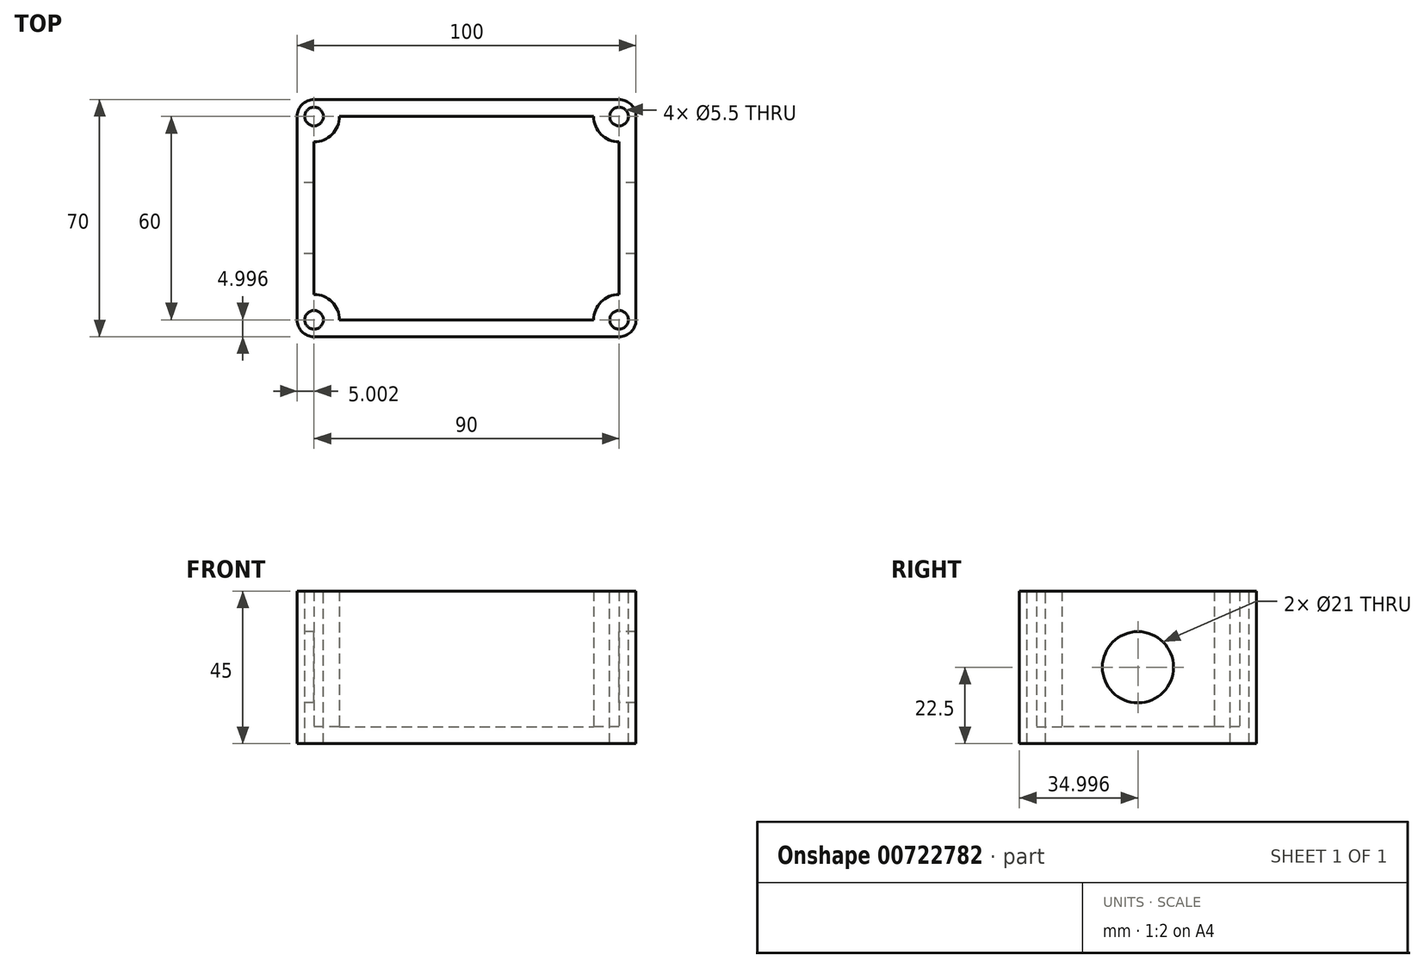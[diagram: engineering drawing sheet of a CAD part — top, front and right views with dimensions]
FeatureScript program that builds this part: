
annotation { "Feature Type Name" : "Feature", "Feature Type Description" : "" }
export const myFeature = defineFeature(function(context is Context, id is Id, definition is map)
    precondition{}
    {
        {
            var Q0;
            Q0=qCreatedBy(makeId("Top.planeOp"),FACE);
            var sketch = newSketch(context, id + "F0", { "sketchPlane" : qUnion([Q0])});
            skLineSegment(sketch, "E0.bottom", {"start": v(-50.44, 34.5) * mm, "end": v(49.56, 34.5) * mm});
            skLineSegment(sketch, "E0.top", {"start": v(-50.44, -35.5) * mm, "end": v(49.56, -35.5) * mm});
            skLineSegment(sketch, "E0.left", {"start": v(-50.44, 34.5) * mm, "end": v(-50.44, -35.5) * mm});
            skLineSegment(sketch, "E0.right", {"start": v(49.56, 34.5) * mm, "end": v(49.56, -35.5) * mm});
            skSolve(sketch);
        }
        {
            var Q0;
            Q0 = qSketchRegion(id + "F0", true);
            extrude(context, id + "F1", {"entities" : qUnion([Q0]), "depth" : 45 * mm, "offsetDistance" : 25 * mm});
        }
        {
            var Q0;
            Q0=makeQuery(id+"F1.opExtrude","CAP_FACE",FACE,{"disambiguationData":[OSD([sQuery(id+"F0.wireOp",EDGE,"E0.bottom"),sQuery(id+"F0.wireOp",EDGE,"E0.top"),sQuery(id+"F0.wireOp",EDGE,"E0.left"),sQuery(id+"F0.wireOp",EDGE,"E0.right")])],"isStart":false});
            shell(context, id + "F2", {"entities" : qUnion([Q0]), "thickness" : 5 * mm});
        }
        {
            var Q0;
            Q0=makeQuery(id+"F2.opShell","OFFSET_FACE",FACE,{"disambiguationData":[OSD([sQuery(id+"F0.wireOp",EDGE,"E0.bottom"),sQuery(id+"F0.wireOp",EDGE,"E0.top"),sQuery(id+"F0.wireOp",EDGE,"E0.left"),sQuery(id+"F0.wireOp",EDGE,"E0.right")])]});
            var sketch = newSketch(context, id + "F3", { "sketchPlane" : qUnion([Q0])});
            skCircle(sketch, "E1", {"center": v(44.56, 29.5) * mm, "radius": 7.5 * mm});
            skCircle(sketch, "E2", {"center": v(44.56, -30.5) * mm, "radius": 7.5 * mm});
            skCircle(sketch, "E3", {"center": v(-45.44, 29.5) * mm, "radius": 7.5 * mm});
            skCircle(sketch, "E4", {"center": v(-45.44, -30.5) * mm, "radius": 7.5 * mm});
            skSolve(sketch);
        }
        {
            var Q0;
            {var subQ0=sQuery(id+"F3.wireOp",EDGE,"E3");var subQ1=sQuery(id+"F0.wireOp",EDGE,"E0.bottom");var subQ2=makeQuery(id+"F2.opShell","OFFSET_EDGE",EDGE,{"disambiguationData":[OSD([subQ1]),TDD([makeQuery(id+"F1.opExtrude","CAP_EDGE",EDGE,{"disambiguationData":[OSD([subQ1])],"isStart":true})])]});var subQ3=makeQuery(id+"F3.imprint","INTERSECT",VERTEX,{"derivedFrom":[subQ2,subQ0]});Q0=makeQuery(id+"F3.imprint","IMPRINT",FACE,{"disambiguationData":[TD([[makeQuery(id+"F3.imprint","IMPRINT",EDGE,{"disambiguationData":[TD([[subQ3,1.0]])],"derivedFrom":subQ0}),1.0]])]});}
            var Q1;
            {var subQ0=sQuery(id+"F3.wireOp",EDGE,"E4");var subQ1=sQuery(id+"F0.wireOp",EDGE,"E0.top");var subQ2=makeQuery(id+"F2.opShell","OFFSET_EDGE",EDGE,{"disambiguationData":[OSD([subQ1]),TDD([makeQuery(id+"F1.opExtrude","CAP_EDGE",EDGE,{"disambiguationData":[OSD([subQ1])],"isStart":true})])]});var subQ3=makeQuery(id+"F3.imprint","INTERSECT",VERTEX,{"derivedFrom":[subQ2,subQ0]});Q1=makeQuery(id+"F3.imprint","IMPRINT",FACE,{"disambiguationData":[TD([[makeQuery(id+"F3.imprint","IMPRINT",EDGE,{"disambiguationData":[TD([[subQ3,-1.0]])],"derivedFrom":subQ0}),1.0]])]});}
            var Q2;
            {var subQ0=sQuery(id+"F3.wireOp",EDGE,"E1");var subQ1=sQuery(id+"F0.wireOp",EDGE,"E0.bottom");var subQ2=makeQuery(id+"F2.opShell","OFFSET_EDGE",EDGE,{"disambiguationData":[OSD([subQ1]),TDD([makeQuery(id+"F1.opExtrude","CAP_EDGE",EDGE,{"disambiguationData":[OSD([subQ1])],"isStart":true})])]});var subQ3=makeQuery(id+"F3.imprint","INTERSECT",VERTEX,{"derivedFrom":[subQ2,subQ0]});Q2=makeQuery(id+"F3.imprint","IMPRINT",FACE,{"disambiguationData":[TD([[makeQuery(id+"F3.imprint","IMPRINT",EDGE,{"disambiguationData":[TD([[subQ3,-1.0]])],"derivedFrom":subQ0}),1.0]])]});}
            var Q3;
            {var subQ0=sQuery(id+"F3.wireOp",EDGE,"E2");var subQ1=sQuery(id+"F0.wireOp",EDGE,"E0.top");var subQ2=makeQuery(id+"F2.opShell","OFFSET_EDGE",EDGE,{"disambiguationData":[OSD([subQ1]),TDD([makeQuery(id+"F1.opExtrude","CAP_EDGE",EDGE,{"disambiguationData":[OSD([subQ1])],"isStart":true})])]});var subQ3=makeQuery(id+"F3.imprint","INTERSECT",VERTEX,{"derivedFrom":[subQ2,subQ0]});Q3=makeQuery(id+"F3.imprint","IMPRINT",FACE,{"disambiguationData":[TD([[makeQuery(id+"F3.imprint","IMPRINT",EDGE,{"disambiguationData":[TD([[subQ3,1.0]])],"derivedFrom":subQ0}),1.0]])]});}
            var Q4;
            Q4=makeQuery(id+"F1.opExtrude","CAP_FACE",FACE,{"disambiguationData":[OSD([sQuery(id+"F0.wireOp",EDGE,"E0.bottom"),sQuery(id+"F0.wireOp",EDGE,"E0.top"),sQuery(id+"F0.wireOp",EDGE,"E0.left"),sQuery(id+"F0.wireOp",EDGE,"E0.right")])],"isStart":false});
            extrude(context, id + "F4", {"entities" : qUnion([Q0, Q1, Q2, Q3]), "operationType" : NewBodyOperationType.ADD, "endBound" : BoundingType.UP_TO_SURFACE, "depth" : 25 * mm, "endBoundEntityFace" : qUnion([Q4]), "offsetDistance" : 25 * mm});
        }
        {
            var Q0;
            {var subQ0=sQuery(id+"F0.wireOp",EDGE,"E0.left");var subQ1=sQuery(id+"F0.wireOp",EDGE,"E0.top");var subQ2=sQuery(id+"F0.wireOp",EDGE,"E0.bottom");var subQ3=sQuery(id+"F0.wireOp",EDGE,"E0.right");Q0=makeQuery(id+"F4.boolean.opBoolean","MERGE",FACE,{"derivedFrom":[makeQuery(id+"F1.opExtrude","CAP_FACE",FACE,{"disambiguationData":[OSD([subQ2,subQ1,subQ0,subQ3])],"isStart":false}),makeQuery(id+"F4.opExtrude","CAP_FACE",FACE,{"disambiguationData":[OSD([subQ2,subQ3,sQuery(id+"F3.wireOp",EDGE,"E1")])],"isStart":false}),makeQuery(id+"F4.opExtrude","CAP_FACE",FACE,{"disambiguationData":[OSD([subQ1,subQ3,sQuery(id+"F3.wireOp",EDGE,"E2")])],"isStart":false}),makeQuery(id+"F4.opExtrude","CAP_FACE",FACE,{"disambiguationData":[OSD([subQ2,subQ0,sQuery(id+"F3.wireOp",EDGE,"E3")])],"isStart":false}),makeQuery(id+"F4.opExtrude","CAP_FACE",FACE,{"disambiguationData":[OSD([subQ1,subQ0,sQuery(id+"F3.wireOp",EDGE,"E4")])],"isStart":false})]});}
            var sketch = newSketch(context, id + "F5", { "sketchPlane" : qUnion([Q0])});
            skLineSegment(sketch, "E5.bottom", {"start": v(44.56, 29.5) * mm, "end": v(-45.44, 29.5) * mm});
            skLineSegment(sketch, "E5.top", {"start": v(44.56, -30.5) * mm, "end": v(-45.44, -30.5) * mm});
            skLineSegment(sketch, "E5.left", {"start": v(44.56, 29.5) * mm, "end": v(44.56, -30.5) * mm});
            skLineSegment(sketch, "E5.right", {"start": v(-45.44, 29.5) * mm, "end": v(-45.44, -30.5) * mm});
            skSolve(sketch);
        }
        {
            var Q0;
            Q0=sQuery(id+"F5.wireOp",VERTEX,"E5.bottom.start");
            var Q1;
            Q1=sQuery(id+"F5.wireOp",VERTEX,"E5.left.end");
            var Q2;
            Q2=sQuery(id+"F5.wireOp",VERTEX,"E5.right.end");
            var Q3;
            Q3=sQuery(id+"F5.wireOp",VERTEX,"E5.bottom.end");
            var Q4;
            Q4=makeQuery(id+"F1.opExtrude","SWEPT_BODY",BODY,{"disambiguationData":[OSD([sQuery(id+"F0.wireOp",EDGE,"E0.bottom"),sQuery(id+"F0.wireOp",EDGE,"E0.top"),sQuery(id+"F0.wireOp",EDGE,"E0.left"),sQuery(id+"F0.wireOp",EDGE,"E0.right")])]});
            hole(context, id + "F6", {"style" : HoleStyle.SIMPLE, "endStyle" : HoleEndStyle.THROUGH, "standardTappedOrClearance" : lookupTablePath({ "standard" : "ISO", "fit" : "Normal", "size" : "M5", "type" : "Clearance" }), "standardBlindInLast" : lookupTablePath({ "fit" : "Standard", "standard" : "ISO", "size" : "M5", "type" : "Clearance" }), "holeDiameter" : 5.5 * mm, "majorDiameter" : 5 * mm, "isTappedThrough" : true, "tappedDepth" : 12 * mm, "tapClearance" : 3, "locations" : qUnion([Q0, Q1, Q2, Q3]), "scope" : qUnion([Q4])});
        }
        {
            var Q0;
            Q0=makeQuery(id+"F1.opExtrude","SWEPT_FACE",FACE,{"disambiguationData":[OSD([sQuery(id+"F0.wireOp",EDGE,"E0.left")])]});
            var sketch = newSketch(context, id + "F7", { "sketchPlane" : qUnion([Q0])});
            skCircle(sketch, "E6", {"center": v(0.5, 22.5) * mm, "radius": 10.5 * mm});
            skPoint(sketch, "E6.centerSnap0", {"position": v(-34.5, 22.5) * mm});
            skPoint(sketch, "E6.centerSnap1", {"position": v(0.5, 45) * mm});
            skSolve(sketch);
        }
        {
            var Q0;
            Q0 = qSketchRegion(id + "F7", true);
            extrude(context, id + "F8", {"entities" : qUnion([Q0]), "operationType" : NewBodyOperationType.REMOVE, "endBound" : BoundingType.THROUGH_ALL, "oppositeDirection" : true, "depth" : 25 * mm, "offsetDistance" : 25 * mm});
        }
        {
            var Q0;
            {var subQ0=sQuery(id+"F0.wireOp",EDGE,"E0.left");var subQ1=sQuery(id+"F0.wireOp",EDGE,"E0.top");var subQ2=sQuery(id+"F0.wireOp",EDGE,"E0.bottom");var subQ3=sQuery(id+"F0.wireOp",EDGE,"E0.right");Q0=makeQuery(id+"F4.boolean.opBoolean","MERGE",FACE,{"derivedFrom":[makeQuery(id+"F1.opExtrude","CAP_FACE",FACE,{"disambiguationData":[OSD([subQ2,subQ1,subQ0,subQ3])],"isStart":false}),makeQuery(id+"F4.opExtrude","CAP_FACE",FACE,{"disambiguationData":[OSD([subQ2,subQ3,sQuery(id+"F3.wireOp",EDGE,"E1")])],"isStart":false}),makeQuery(id+"F4.opExtrude","CAP_FACE",FACE,{"disambiguationData":[OSD([subQ1,subQ3,sQuery(id+"F3.wireOp",EDGE,"E2")])],"isStart":false}),makeQuery(id+"F4.opExtrude","CAP_FACE",FACE,{"disambiguationData":[OSD([subQ2,subQ0,sQuery(id+"F3.wireOp",EDGE,"E3")])],"isStart":false}),makeQuery(id+"F4.opExtrude","CAP_FACE",FACE,{"disambiguationData":[OSD([subQ1,subQ0,sQuery(id+"F3.wireOp",EDGE,"E4")])],"isStart":false})]});}
            var sketch = newSketch(context, id + "F9", { "sketchPlane" : qUnion([Q0])});
            skLineSegment(sketch, "E7.0", {"start": v(-52.44, 36.5) * mm, "end": v(-52.44, -37.5) * mm});
            skLineSegment(sketch, "E7.1", {"start": v(51.56, 36.5) * mm, "end": v(-52.44, 36.5) * mm});
            skLineSegment(sketch, "E7.2", {"start": v(51.56, -37.5) * mm, "end": v(51.56, 36.5) * mm});
            skLineSegment(sketch, "E7.3", {"start": v(-52.44, -37.5) * mm, "end": v(51.56, -37.5) * mm});
            skSolve(sketch);
        }
        {
            var Q0;
            Q0=makeQuery(id+"F1.opExtrude","SWEPT_EDGE",EDGE,{"disambiguationData":[OSD([sQuery(id+"F0.wireOp",EDGE,"E0.bottom"),sQuery(id+"F0.wireOp",EDGE,"E0.left")])]});
            var Q1;
            Q1=makeQuery(id+"F1.opExtrude","SWEPT_EDGE",EDGE,{"disambiguationData":[OSD([sQuery(id+"F0.wireOp",EDGE,"E0.bottom"),sQuery(id+"F0.wireOp",EDGE,"E0.right")])]});
            var Q2;
            Q2=makeQuery(id+"F1.opExtrude","SWEPT_EDGE",EDGE,{"disambiguationData":[OSD([sQuery(id+"F0.wireOp",EDGE,"E0.top"),sQuery(id+"F0.wireOp",EDGE,"E0.left")])]});
            var Q3;
            Q3=makeQuery(id+"F1.opExtrude","SWEPT_EDGE",EDGE,{"disambiguationData":[OSD([sQuery(id+"F0.wireOp",EDGE,"E0.top"),sQuery(id+"F0.wireOp",EDGE,"E0.right")])]});
            fillet(context, id + "F10", {"entities" : qUnion([Q0, Q1, Q2, Q3]), "radius" : 5 * mm, "tangentPropagation" : true, "allowEdgeOverflow" : false});
        }
    });
